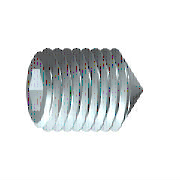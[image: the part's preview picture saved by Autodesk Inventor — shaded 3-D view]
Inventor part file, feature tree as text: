
AUTODESK INVENTOR PART (.ipt)
format: ipt  version: 2023.3 (Build 273359000, 359)  size: 164,352 bytes
history: native  units: mm (DEFAULTED — no unit token found)
features: other x2, sketch x2, extrude x1, plane x1
ambient origin geometry x8: Origin, YZ Plane, XZ Plane, XY Plane, X Axis, Y Axis, Z Axis, Center Point
bodies: Solid1 (feature_tree)
feature tree (6):
  other  "Körper"
  extrude  "Loch"  TaperAngle=60.0deg  [1 undecoded]
  other  "Work Axis1"
  plane  "Work Plane1"
  sketch  "Skizze1"  dims[d0=0.8mm d1=60.0deg]
  sketch  "Skizze2"  dims[d2=2.0mm d3=1.03923mm d6=90.0deg d4=0.0mm d5=2.5mm d21=10.0mm d7=0.0mm d8=0.433013mm d9=60.0deg d10=0.24538mm d11=60.0deg d12=2.5mm d13=0.0mm d34=0.433013mm d35=0.24538mm d36=0.0mm d37=0.0mm]
note: 1 required parameter value undecoded (feature->parameter linkage not recoverable at this tier; creation-order binding heuristic only, values carry confidence <= 0.55)
